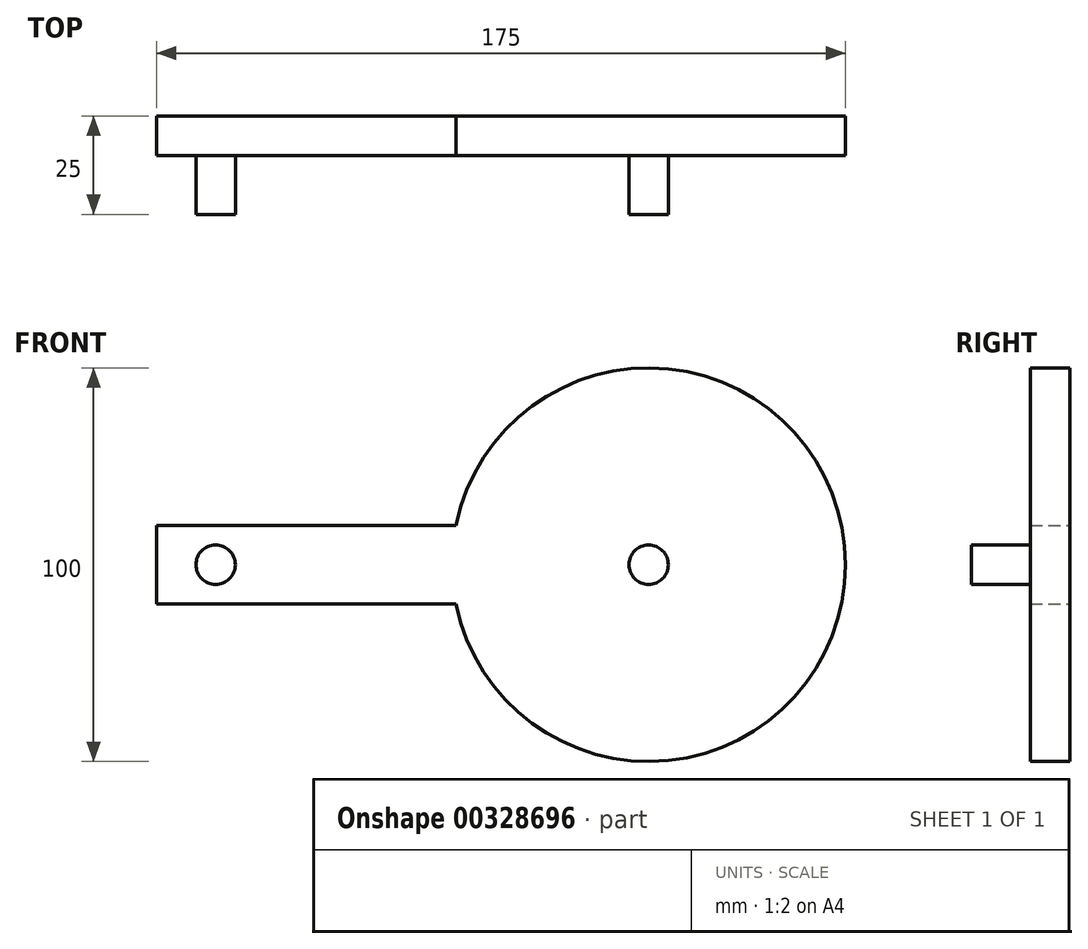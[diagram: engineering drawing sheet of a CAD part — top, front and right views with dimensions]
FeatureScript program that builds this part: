
annotation { "Feature Type Name" : "Feature", "Feature Type Description" : "" }
export const myFeature = defineFeature(function(context is Context, id is Id, definition is map)
    precondition{}
    {
        {
            var Q0;
            Q0=qCreatedBy(makeId("Front.planeOp"),FACE);
            var sketch = newSketch(context, id + "F0", { "sketchPlane" : qUnion([Q0])});
            skCircle(sketch, "E0", {"center": v(0, 0) * mm, "radius": 50 * mm});
            skCircle(sketch, "E1", {"center": v(0, 0) * mm, "radius": 60 * mm, "construction": true});
            skCircle(sketch, "E2", {"center": v(-110, 0) * mm, "radius": 50 * mm, "construction": true});
            skLineSegment(sketch, "E3", {"start": v(-64.55, 20.83) * mm, "end": v(-45.45, -20.83) * mm, "construction": true});
            skArc(sketch, "E4", {"start": v(-59.92, -3.06) * mm, "mid": v(-57.56, -1.37) * mm, "end": v(-55, 0) * mm});
            skArc(sketch, "E5", {"start": v(-55, 0) * mm, "mid": v(-52.53, 0.96) * mm, "end": v(-49.97, 1.63) * mm});
            skLineSegment(sketch, "E6", {"start": v(-59.92, -3.06) * mm, "end": v(-45.45, -20.83) * mm});
            skCircle(sketch, "E7", {"center": v(0, 0) * mm, "radius": 5 * mm});
            skCircle(sketch, "E8", {"center": v(-110, 0) * mm, "radius": 5 * mm});
            skLineSegment(sketch, "E9.bottom", {"start": v(-125, -10) * mm, "end": v(15, -10) * mm});
            skLineSegment(sketch, "E9.top", {"start": v(-125, 10) * mm, "end": v(15, 10) * mm});
            skLineSegment(sketch, "E9.left", {"start": v(-125, -10) * mm, "end": v(-125, 10) * mm});
            skLineSegment(sketch, "E9.right", {"start": v(15, -10) * mm, "end": v(15, 10) * mm});
            skLineSegment(sketch, "E10", {"start": v(-110, 0) * mm, "end": v(0, 0) * mm, "construction": true});
            skSolve(sketch);
        }
        {
            var Q0;
            {var subQ0=sQuery(id+"F0.wireOp",EDGE,"E9.right");Q0=makeQuery(id+"F0.imprint","IMPRINT",FACE,{"disambiguationData":[TD([[makeQuery(id+"F0.imprint","IMPRINT",EDGE,{"derivedFrom":subQ0}),-1.0]])]});}
            var Q1;
            Q1=makeQuery(id+"F0.imprint","IMPRINT",FACE,{"disambiguationData":[TD([[makeQuery(id+"F0.imprint","IMPRINT",EDGE,{"derivedFrom":sQuery(id+"F0.wireOp",EDGE,"E7")}),-1.0]])]});
            var Q2;
            {var subQ1=sQuery(id+"F0.wireOp",EDGE,"E4");Q2=makeQuery(id+"F0.imprint","IMPRINT",FACE,{"disambiguationData":[TD([[makeQuery(id+"F0.imprint","IMPRINT",EDGE,{"derivedFrom":subQ1}),-1.0]])]});}
            extrude(context, id + "F1", {"entities" : qUnion([Q0, Q1, Q2]), "depth" : 10 * mm});
        }
        {
            var Q0;
            {var subQ1=sQuery(id+"F0.wireOp",EDGE,"E4");Q0=makeQuery(id+"F0.imprint","IMPRINT",FACE,{"disambiguationData":[TD([[makeQuery(id+"F0.imprint","IMPRINT",EDGE,{"derivedFrom":subQ1}),1.0]])]});}
            var Q1;
            Q1=makeQuery(id+"F0.imprint","IMPRINT",FACE,{"disambiguationData":[TD([[makeQuery(id+"F0.imprint","IMPRINT",EDGE,{"derivedFrom":sQuery(id+"F0.wireOp",EDGE,"E7")}),-1.0]])]});
            var Q2;
            {var subQ1=sQuery(id+"F0.wireOp",EDGE,"E4");Q2=makeQuery(id+"F0.imprint","IMPRINT",FACE,{"disambiguationData":[TD([[makeQuery(id+"F0.imprint","IMPRINT",EDGE,{"derivedFrom":subQ1}),-1.0]])]});}
            var Q3;
            Q3=makeQuery(id+"F0.imprint","IMPRINT",FACE,{"disambiguationData":[TD([[makeQuery(id+"F0.imprint","IMPRINT",EDGE,{"derivedFrom":sQuery(id+"F0.wireOp",EDGE,"E8")}),1.0]])]});
            var Q4;
            Q4=makeQuery(id+"F0.imprint","IMPRINT",FACE,{"disambiguationData":[TD([[makeQuery(id+"F0.imprint","IMPRINT",EDGE,{"derivedFrom":sQuery(id+"F0.wireOp",EDGE,"E7")}),1.0]])]});
            extrude(context, id + "F2", {"entities" : qUnion([Q0, Q1, Q2, Q3, Q4]), "depth" : 10 * mm});
        }
        {
            var Q0;
            Q0=makeQuery(id+"F0.imprint","IMPRINT",FACE,{"disambiguationData":[TD([[makeQuery(id+"F0.imprint","IMPRINT",EDGE,{"derivedFrom":sQuery(id+"F0.wireOp",EDGE,"E8")}),1.0]])]});
            var Q1;
            Q1=makeQuery(id+"F0.imprint","IMPRINT",FACE,{"disambiguationData":[TD([[makeQuery(id+"F0.imprint","IMPRINT",EDGE,{"derivedFrom":sQuery(id+"F0.wireOp",EDGE,"E7")}),1.0]])]});
            var Q2;
            Q2=sQuery(id+"F0.wireOp",EDGE,"E8");
            var Q3;
            Q3=sQuery(id+"F0.wireOp",EDGE,"E7");
            extrude(context, id + "F3", {"entities" : qUnion([Q0, Q1]), "operationType" : NewBodyOperationType.ADD, "surfaceEntities" : qUnion([Q2, Q3]), "depth" : 25 * mm});
        }
    });
